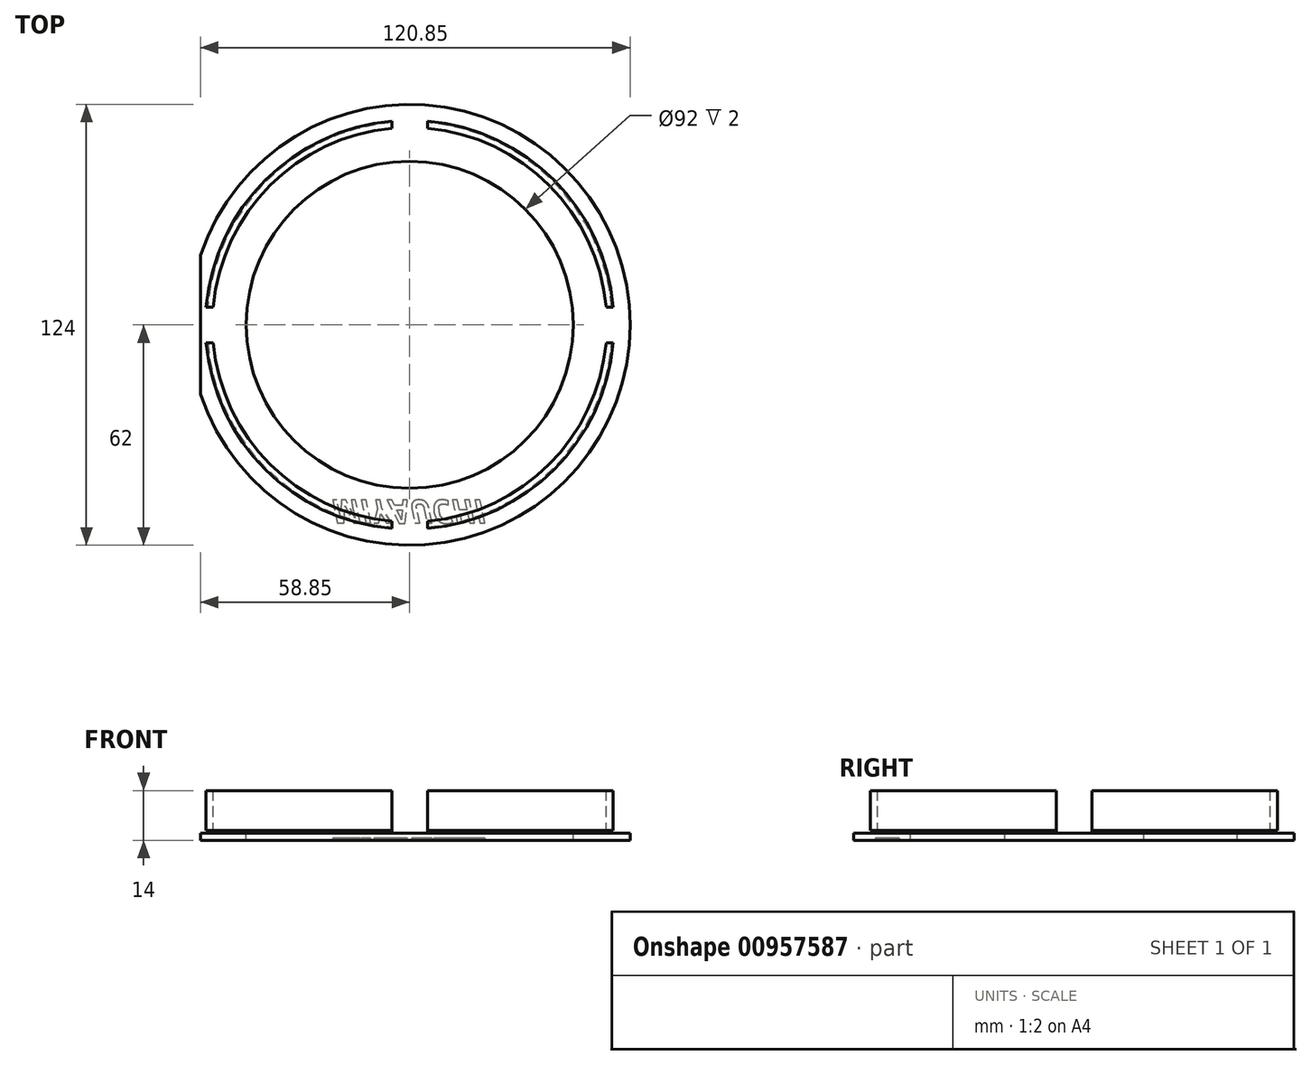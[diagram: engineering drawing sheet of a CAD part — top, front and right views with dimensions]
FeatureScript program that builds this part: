
annotation { "Feature Type Name" : "Feature", "Feature Type Description" : "" }
export const myFeature = defineFeature(function(context is Context, id is Id, definition is map)
    precondition{}
    {
        {
            var Q0;
            Q0=qCreatedBy(makeId("Top.planeOp"),FACE);
            var sketch = newSketch(context, id + "F0", { "sketchPlane" : qUnion([Q0])});
            skCircle(sketch, "E0", {"center": v(0, 0) * mm, "radius": 62 * mm});
            skSolve(sketch);
        }
        {
            var Q0;
            Q0=qSketchRegion(id+"F0",true);
            extrude(context, id + "F1", {"entities" : qUnion([Q0]), "depth" : 2 * mm, "offsetDistance" : 25 * mm});
        }
        {
            var Q0;
            Q0=makeQuery(id+"F1.opExtrude","CAP_FACE",FACE,{"disambiguationData":[OSD([sQuery(id+"F0.wireOp",EDGE,"E0")])],"isStart":false});
            var sketch = newSketch(context, id + "F2", { "sketchPlane" : qUnion([Q0])});
            skCircle(sketch, "E1", {"center": v(0, 0) * mm, "radius": 57.5 * mm});
            skSolve(sketch);
        }
        {
            var Q0;
            Q0=qSketchRegion(id+"F2",true);
            extrude(context, id + "F3", {"entities" : qUnion([Q0]), "operationType" : NewBodyOperationType.ADD, "depth" : 2 * mm, "offsetDistance" : 25 * mm});
        }
        {
            var Q0;
            Q0=makeQuery(id+"F3.opExtrude","CAP_FACE",FACE,{"disambiguationData":[OSD([sQuery(id+"F2.wireOp",EDGE,"E1")])],"isStart":false});
            var sketch = newSketch(context, id + "F4", { "sketchPlane" : qUnion([Q0])});
            skCircle(sketch, "E2", {"center": v(0, 0) * mm, "radius": 55.5 * mm});
            skSolve(sketch);
        }
        {
            var Q0;
            Q0=makeQuery(id+"F1.opExtrude","CAP_FACE",FACE,{"disambiguationData":[OSD([sQuery(id+"F0.wireOp",EDGE,"E0")])],"isStart":false});
            var sketch = newSketch(context, id + "F5", { "sketchPlane" : qUnion([Q0])});
            skLineSegment(sketch, "E3.bottom", {"start": v(-72.95, 40.58) * mm, "end": v(-58.85, 40.58) * mm});
            skLineSegment(sketch, "E3.top", {"start": v(-72.95, -45.22) * mm, "end": v(-58.85, -45.22) * mm});
            skLineSegment(sketch, "E3.left", {"start": v(-72.95, 40.58) * mm, "end": v(-72.95, -45.22) * mm});
            skLineSegment(sketch, "E3.right", {"start": v(-58.85, 40.58) * mm, "end": v(-58.85, -45.22) * mm});
            skSolve(sketch);
        }
        {
            var Q0;
            Q0=qSketchRegion(id+"F5",true);
            extrude(context, id + "F6", {"entities" : qUnion([Q0]), "operationType" : NewBodyOperationType.REMOVE, "oppositeDirection" : true, "depth" : 25 * mm, "offsetDistance" : 25 * mm});
        }
        {
            var Q0;
            Q0=makeQuery(id+"F4.imprint","IMPRINT",FACE,{"disambiguationData":[TD([[makeQuery(id+"F4.imprint","IMPRINT",EDGE,{"derivedFrom":sQuery(id+"F4.wireOp",EDGE,"E2")}),1.0]])]});
            var Q1;
            Q1=makeQuery(id+"FJXupGKDpmXe2a8_1.boolean.opBoolean","MERGE",FACE,{"derivedFrom":[makeQuery(id+"FN44vK6vQmVlS3t_1.boolean.opBoolean","MERGE",FACE,{"derivedFrom":[makeQuery(id+"F3.opExtrude","CAP_FACE",FACE,{"disambiguationData":[OSD([sQuery(id+"F2.wireOp",EDGE,"E1")])],"isStart":false}),makeQuery(id+"FN44vK6vQmVlS3t_1.opExtrude","CAP_FACE",FACE,{"disambiguationData":[OSD([sQuery(id+"FNXWfjMKIt4FYrd_1.wireOp",EDGE,"77dzCXSC-6Dvt-BKk6-6YgZ-W8trsqLhyYVH.bottom"),sQuery(id+"FNXWfjMKIt4FYrd_1.wireOp",EDGE,"77dzCXSC-6Dvt-BKk6-6YgZ-W8trsqLhyYVH.top"),sQuery(id+"FNXWfjMKIt4FYrd_1.wireOp",EDGE,"77dzCXSC-6Dvt-BKk6-6YgZ-W8trsqLhyYVH.left"),sQuery(id+"FNXWfjMKIt4FYrd_1.wireOp",EDGE,"77dzCXSC-6Dvt-BKk6-6YgZ-W8trsqLhyYVH.right")])],"isStart":true})]}),makeQuery(id+"FJXupGKDpmXe2a8_1.opExtrude","CAP_FACE",FACE,{"disambiguationData":[OSD([sQuery(id+"FRo1LvYlPspa8ka_1.wireOp",EDGE,"mKYJYvvI-SVSM-CQjT-eOTL-3OLUUcy5syB3.bottom"),sQuery(id+"FRo1LvYlPspa8ka_1.wireOp",EDGE,"mKYJYvvI-SVSM-CQjT-eOTL-3OLUUcy5syB3.top"),sQuery(id+"FRo1LvYlPspa8ka_1.wireOp",EDGE,"mKYJYvvI-SVSM-CQjT-eOTL-3OLUUcy5syB3.left"),sQuery(id+"FRo1LvYlPspa8ka_1.wireOp",EDGE,"mKYJYvvI-SVSM-CQjT-eOTL-3OLUUcy5syB3.right")])],"isStart":true})]});
            var Q2;
            Q2=makeQuery(id+"F1.opExtrude","CAP_FACE",FACE,{"disambiguationData":[OSD([sQuery(id+"F0.wireOp",EDGE,"E0")])],"isStart":true});
            extrude(context, id + "F7", {"entities" : qUnion([Q0, Q1, Q2]), "operationType" : NewBodyOperationType.REMOVE, "oppositeDirection" : true, "depth" : 2 * mm, "offsetDistance" : 25 * mm});
        }
        {
            var Q0;
            Q0=makeQuery(id+"F7.boolean.opBoolean","MERGE",FACE,{"derivedFrom":[makeQuery(id+"F1.opExtrude","CAP_FACE",FACE,{"disambiguationData":[OSD([sQuery(id+"F0.wireOp",EDGE,"E0")])],"isStart":false})],"fromTools":[makeQuery(id+"F7.opExtrude","CAP_FACE",FACE,{"disambiguationData":[OSD([sQuery(id+"F4.wireOp",EDGE,"E2")])],"isStart":false}),makeQuery(id+"F7.opExtrude","CAP_FACE",FACE,{"disambiguationData":[OSD([sQuery(id+"F2.wireOp",EDGE,"E1"),sQuery(id+"FNXWfjMKIt4FYrd_1.wireOp",EDGE,"77dzCXSC-6Dvt-BKk6-6YgZ-W8trsqLhyYVH.bottom"),sQuery(id+"FNXWfjMKIt4FYrd_1.wireOp",EDGE,"77dzCXSC-6Dvt-BKk6-6YgZ-W8trsqLhyYVH.top"),sQuery(id+"FNXWfjMKIt4FYrd_1.wireOp",EDGE,"77dzCXSC-6Dvt-BKk6-6YgZ-W8trsqLhyYVH.left"),sQuery(id+"FNXWfjMKIt4FYrd_1.wireOp",EDGE,"77dzCXSC-6Dvt-BKk6-6YgZ-W8trsqLhyYVH.right"),sQuery(id+"FRo1LvYlPspa8ka_1.wireOp",EDGE,"mKYJYvvI-SVSM-CQjT-eOTL-3OLUUcy5syB3.bottom"),sQuery(id+"FRo1LvYlPspa8ka_1.wireOp",EDGE,"mKYJYvvI-SVSM-CQjT-eOTL-3OLUUcy5syB3.top"),sQuery(id+"FRo1LvYlPspa8ka_1.wireOp",EDGE,"mKYJYvvI-SVSM-CQjT-eOTL-3OLUUcy5syB3.left"),sQuery(id+"FRo1LvYlPspa8ka_1.wireOp",EDGE,"mKYJYvvI-SVSM-CQjT-eOTL-3OLUUcy5syB3.right")])],"isStart":false})]});
            var sketch = newSketch(context, id + "F8", { "sketchPlane" : qUnion([Q0])});
            skCircle(sketch, "E4", {"center": v(0, 0) * mm, "radius": 57.1 * mm});
            skSolve(sketch);
        }
        {
            var Q0;
            Q0 = qSketchRegion(id + "F8", true);
            extrude(context, id + "F9", {"entities" : qUnion([Q0]), "operationType" : NewBodyOperationType.ADD, "depth" : .8 * mm, "offsetDistance" : 25 * mm});
        }
        {
            var Q0;
            Q0=makeQuery(id+"F9.opExtrude","CAP_FACE",FACE,{"disambiguationData":[OSD([sQuery(id+"F8.wireOp",EDGE,"E4")])],"isStart":false});
            var sketch = newSketch(context, id + "F10", { "sketchPlane" : qUnion([Q0])});
            skCircle(sketch, "E5", {"center": v(0, 0) * mm, "radius": 57.5 * mm});
            skSolve(sketch);
        }
        {
            var Q0;
            Q0 = qSketchRegion(id + "F10", true);
            extrude(context, id + "F11", {"entities" : qUnion([Q0]), "operationType" : NewBodyOperationType.ADD, "depth" : (12 - .8) * mm, "offsetDistance" : 25 * mm});
        }
        {
            var Q0;
            Q0=makeQuery(id+"F11.opExtrude","CAP_FACE",FACE,{"disambiguationData":[OSD([sQuery(id+"F10.wireOp",EDGE,"E5")])],"isStart":false});
            var sketch = newSketch(context, id + "F12", { "sketchPlane" : qUnion([Q0])});
            skCircle(sketch, "E6", {"center": v(0, 0) * mm, "radius": 46 * mm});
            skSolve(sketch);
        }
        {
            var Q0;
            Q0 = qSketchRegion(id + "F12", true);
            extrude(context, id + "F13", {"entities" : qUnion([Q0]), "operationType" : NewBodyOperationType.REMOVE, "oppositeDirection" : true, "depth" : 25 * mm, "offsetDistance" : 25 * mm});
        }
        {
            var Q0;
            Q0=makeQuery(id+"F11.opExtrude","CAP_FACE",FACE,{"disambiguationData":[OSD([sQuery(id+"F10.wireOp",EDGE,"E5")])],"isStart":false});
            var sketch = newSketch(context, id + "F14", { "sketchPlane" : qUnion([Q0])});
            skCircle(sketch, "E7", {"center": v(0, 0) * mm, "radius": 55.5 * mm});
            skSolve(sketch);
        }
        {
            var Q0;
            Q0 = qSketchRegion(id + "F14", true);
            extrude(context, id + "F15", {"entities" : qUnion([Q0]), "operationType" : NewBodyOperationType.REMOVE, "oppositeDirection" : true, "depth" : 12 * mm, "offsetDistance" : 25 * mm});
        }
        {
            var Q0;
            Q0=makeQuery(id+"F11.opExtrude","CAP_FACE",FACE,{"disambiguationData":[OSD([sQuery(id+"F10.wireOp",EDGE,"E5")])],"isStart":false});
            var sketch = newSketch(context, id + "F16", { "sketchPlane" : qUnion([Q0])});
            skLineSegment(sketch, "E8.bottom", {"start": v(-5, 60) * mm, "end": v(5, 60) * mm});
            skLineSegment(sketch, "E8.top", {"start": v(-5, -60) * mm, "end": v(5, -60) * mm});
            skLineSegment(sketch, "E8.left", {"start": v(-5, 60) * mm, "end": v(-5, -60) * mm});
            skLineSegment(sketch, "E8.right", {"start": v(5, 60) * mm, "end": v(5, -60) * mm});
            skPoint(sketch, "E8.middle", {"position": v(0, 0) * mm});
            skSolve(sketch);
        }
        {
            var Q0;
            Q0 = qSketchRegion(id + "F16", true);
            extrude(context, id + "F17", {"entities" : qUnion([Q0]), "operationType" : NewBodyOperationType.REMOVE, "oppositeDirection" : true, "depth" : 12 * mm, "offsetDistance" : 25 * mm});
        }
        {
            var Q0;
            {var subQ0=sQuery(id+"F10.wireOp",EDGE,"E5");Q0=makeQuery(id+"F17.boolean.opBoolean","SPLIT",FACE,{"disambiguationData":[TD([makeQuery(id+"F17.opExtrude","SWEPT_FACE",FACE,{"disambiguationData":[OSD([sQuery(id+"F16.wireOp",EDGE,"E8.left")])]})])],"derivedFrom":makeQuery(id+"F11.opExtrude","CAP_FACE",FACE,{"disambiguationData":[OSD([subQ0])],"isStart":false})});}
            var sketch = newSketch(context, id + "F18", { "sketchPlane" : qUnion([Q0])});
            skLineSegment(sketch, "E9.bottom", {"start": v(-60, 5) * mm, "end": v(60, 5) * mm});
            skLineSegment(sketch, "E9.top", {"start": v(-60, -5) * mm, "end": v(60, -5) * mm});
            skLineSegment(sketch, "E9.left", {"start": v(-60, 5) * mm, "end": v(-60, -5) * mm});
            skLineSegment(sketch, "E9.right", {"start": v(60, 5) * mm, "end": v(60, -5) * mm});
            skPoint(sketch, "E9.middle", {"position": v(0, 0) * mm});
            skSolve(sketch);
        }
        {
            var Q0;
            Q0 = qSketchRegion(id + "F18", true);
            extrude(context, id + "F19", {"entities" : qUnion([Q0]), "operationType" : NewBodyOperationType.REMOVE, "oppositeDirection" : true, "depth" : 12 * mm, "offsetDistance" : 25 * mm});
        }
        {
            var Q0;
            Q0=makeQuery(id+"F1.opExtrude","CAP_FACE",FACE,{"disambiguationData":[OSD([sQuery(id+"F0.wireOp",EDGE,"E0")])],"isStart":true});
            var sketch = newSketch(context, id + "F20", { "sketchPlane" : qUnion([Q0])});
            skText(sketch, "E10", { "text": "MIYAUCHI", "fontName": "OpenSans-BoldItalic.ttf"});
            const initialGuessF20  = {"E10": [-0.02193, 0.04928, 1, 0, 0.00657]};
            skSetInitialGuess(sketch, initialGuessF20);
            skSolve(sketch);
        }
        {
            var Q0;
            Q0 = qSketchRegion(id + "F20", true);
            extrude(context, id + "F21", {"entities" : qUnion([Q0]), "operationType" : NewBodyOperationType.REMOVE, "oppositeDirection" : true, "depth" : 0.6 * mm, "offsetDistance" : 25 * mm});
        }
    });
